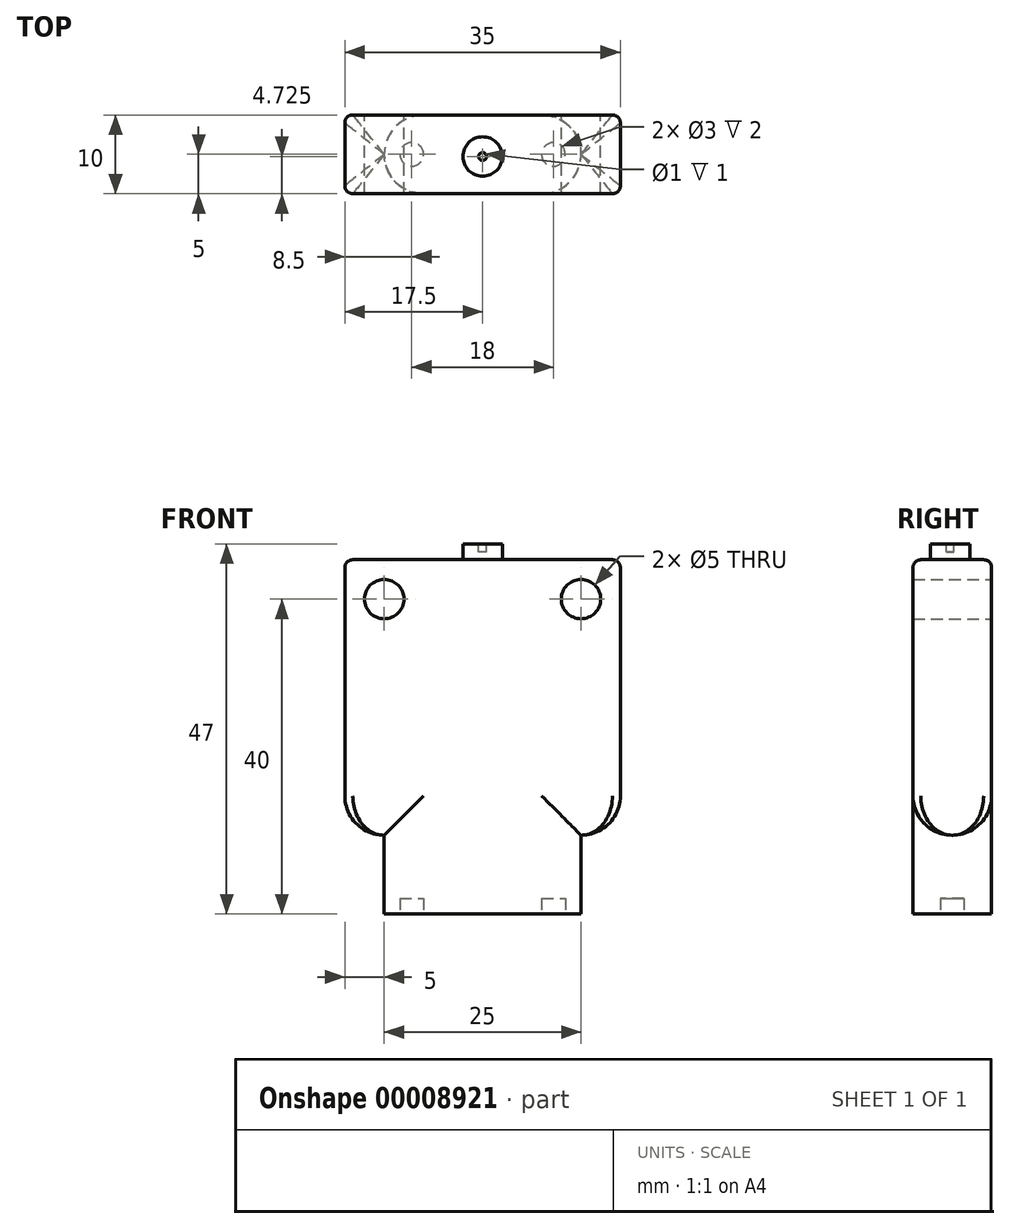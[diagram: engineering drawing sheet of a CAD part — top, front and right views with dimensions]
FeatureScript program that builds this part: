
annotation { "Feature Type Name" : "Feature", "Feature Type Description" : "" }
export const myFeature = defineFeature(function(context is Context, id is Id, definition is map)
    precondition{}
    {
        {
            var Q0;
            Q0=qCreatedBy(makeId("Top.planeOp"),FACE);
            var sketch = newSketch(context, id + "F0", { "sketchPlane" : qUnion([Q0])});
            skLineSegment(sketch, "E0.bottom", {"start": v(0, 0) * mm, "end": v(-25, 0) * mm});
            skLineSegment(sketch, "E0.top", {"start": v(0, 10) * mm, "end": v(-25, 10) * mm});
            skLineSegment(sketch, "E0.left", {"start": v(0, 0) * mm, "end": v(0, 10) * mm});
            skLineSegment(sketch, "E0.right", {"start": v(-25, 0) * mm, "end": v(-25, 10) * mm});
            skSolve(sketch);
        }
        {
            var Q0;
            Q0 = qSketchRegion(id + "F0", true);
            extrude(context, id + "F1", {"entities" : qUnion([Q0]), "depth" : 10 * mm});
        }
        {
            var Q0;
            Q0=makeQuery(id+"F1.opExtrude","CAP_FACE",FACE,{"disambiguationData":[OSD([sQuery(id+"F0.wireOp",EDGE,"E0.bottom"),sQuery(id+"F0.wireOp",EDGE,"E0.top"),sQuery(id+"F0.wireOp",EDGE,"E0.left"),sQuery(id+"F0.wireOp",EDGE,"E0.right")])],"isStart":true});
            var sketch = newSketch(context, id + "F2", { "sketchPlane" : qUnion([Q0])});
            skCircle(sketch, "E1", {"center": v(-21.5, -5) * mm, "radius": 1.5 * mm});
            skCircle(sketch, "E2", {"center": v(-3.5, -5) * mm, "radius": 1.5 * mm});
            skSolve(sketch);
        }
        {
            var Q0;
            Q0 = qSketchRegion(id + "F2", true);
            extrude(context, id + "F3", {"entities" : qUnion([Q0]), "operationType" : NewBodyOperationType.REMOVE, "oppositeDirection" : true, "depth" : 2 * mm});
        }
        {
            var Q0;
            Q0=makeQuery(id+"F1.opExtrude","SWEPT_EDGE",EDGE,{"disambiguationData":[OSD([sQuery(id+"F0.wireOp",EDGE,"E0.bottom"),sQuery(id+"F0.wireOp",EDGE,"E0.right")])]});
            var Q1;
            Q1=makeQuery(id+"F1.opExtrude","SWEPT_EDGE",EDGE,{"disambiguationData":[OSD([sQuery(id+"F0.wireOp",EDGE,"E0.top"),sQuery(id+"F0.wireOp",EDGE,"E0.right")])]});
            var Q2;
            Q2=makeQuery(id+"F1.opExtrude","SWEPT_EDGE",EDGE,{"disambiguationData":[OSD([sQuery(id+"F0.wireOp",EDGE,"E0.bottom"),sQuery(id+"F0.wireOp",EDGE,"E0.left")])]});
            var Q3;
            Q3=makeQuery(id+"F1.opExtrude","SWEPT_EDGE",EDGE,{"disambiguationData":[OSD([sQuery(id+"F0.wireOp",EDGE,"E0.top"),sQuery(id+"F0.wireOp",EDGE,"E0.left")])]});
            fillet(context, id + "F4", {"entities" : qUnion([Q0, Q1, Q2, Q3]), "radius" : 5 * mm, "tangentPropagation" : true, "allowEdgeOverflow" : false});
        }
        {
            var Q0;
            Q0=qCreatedBy(makeId("Front.planeOp"),FACE);
            var sketch = newSketch(context, id + "F5", { "sketchPlane" : qUnion([Q0])});
            skLineSegment(sketch, "E3.bottom", {"start": v(5, 10) * mm, "end": v(-30, 10) * mm});
            skLineSegment(sketch, "E3.top", {"start": v(5, 45) * mm, "end": v(-30, 45) * mm});
            skLineSegment(sketch, "E3.left", {"start": v(5, 10) * mm, "end": v(5, 45) * mm});
            skLineSegment(sketch, "E3.right", {"start": v(-30, 10) * mm, "end": v(-30, 45) * mm});
            skSolve(sketch);
        }
        {
            var Q0;
            Q0 = qSketchRegion(id + "F5", true);
            extrude(context, id + "F6", {"entities" : qUnion([Q0]), "operationType" : NewBodyOperationType.ADD, "oppositeDirection" : true, "depth" : 10 * mm});
        }
        {
            var Q0;
            {var subQ0=sQuery(id+"F5.wireOp",EDGE,"E3.bottom");var subQ1=sQuery(id+"F5.wireOp",EDGE,"E3.left");Q0=makeQuery(id+"F6.boolean.opBoolean","SPLIT",EDGE,{"disambiguationData":[TD([makeQuery(id+"F6.opExtrude","SWEPT_FACE",FACE,{"disambiguationData":[OSD([subQ1])]})])],"derivedFrom":makeQuery(id+"F6.opExtrude","CAP_EDGE",EDGE,{"disambiguationData":[OSD([subQ0])],"isStart":false})});}
            var Q1;
            {var subQ0=sQuery(id+"F5.wireOp",EDGE,"E3.bottom");var subQ1=sQuery(id+"F5.wireOp",EDGE,"E3.left");Q1=makeQuery(id+"F6.boolean.opBoolean","SPLIT",EDGE,{"disambiguationData":[TD([makeQuery(id+"F6.opExtrude","SWEPT_FACE",FACE,{"disambiguationData":[OSD([subQ1])]})])],"derivedFrom":makeQuery(id+"F6.opExtrude","CAP_EDGE",EDGE,{"disambiguationData":[OSD([subQ0])],"isStart":true})});}
            var Q2;
            {var subQ0=sQuery(id+"F5.wireOp",EDGE,"E3.bottom");var subQ1=sQuery(id+"F5.wireOp",EDGE,"E3.right");Q2=makeQuery(id+"F6.boolean.opBoolean","SPLIT",EDGE,{"disambiguationData":[TD([makeQuery(id+"F6.opExtrude","SWEPT_FACE",FACE,{"disambiguationData":[OSD([subQ1])]})])],"derivedFrom":makeQuery(id+"F6.opExtrude","CAP_EDGE",EDGE,{"disambiguationData":[OSD([subQ0])],"isStart":false})});}
            var Q3;
            {var subQ0=sQuery(id+"F5.wireOp",EDGE,"E3.bottom");var subQ1=sQuery(id+"F5.wireOp",EDGE,"E3.right");Q3=makeQuery(id+"F6.boolean.opBoolean","SPLIT",EDGE,{"disambiguationData":[TD([makeQuery(id+"F6.opExtrude","SWEPT_FACE",FACE,{"disambiguationData":[OSD([subQ1])]})])],"derivedFrom":makeQuery(id+"F6.opExtrude","CAP_EDGE",EDGE,{"disambiguationData":[OSD([subQ0])],"isStart":true})});}
            var Q4;
            Q4=makeQuery(id+"F6.opExtrude","SWEPT_EDGE",EDGE,{"disambiguationData":[OSD([sQuery(id+"F5.wireOp",EDGE,"E3.bottom"),sQuery(id+"F5.wireOp",EDGE,"E3.left")])]});
            var Q5;
            Q5=makeQuery(id+"F6.opExtrude","SWEPT_EDGE",EDGE,{"disambiguationData":[OSD([sQuery(id+"F5.wireOp",EDGE,"E3.bottom"),sQuery(id+"F5.wireOp",EDGE,"E3.right")])]});
            fillet(context, id + "F7", {"entities" : qUnion([Q0, Q1, Q2, Q3, Q4, Q5]), "radius" : 5 * mm, "tangentPropagation" : true, "allowEdgeOverflow" : false});
        }
        {
            var Q0;
            Q0=makeQuery(id+"F6.boolean.opBoolean","MERGE",FACE,{"derivedFrom":[makeQuery(id+"F1.opExtrude","SWEPT_FACE",FACE,{"disambiguationData":[OSD([sQuery(id+"F0.wireOp",EDGE,"E0.top")])]}),makeQuery(id+"F6.opExtrude","CAP_FACE",FACE,{"disambiguationData":[OSD([sQuery(id+"F5.wireOp",EDGE,"E3.bottom"),sQuery(id+"F5.wireOp",EDGE,"E3.top"),sQuery(id+"F5.wireOp",EDGE,"E3.left"),sQuery(id+"F5.wireOp",EDGE,"E3.right")])],"isStart":false})]});
            var sketch = newSketch(context, id + "F8", { "sketchPlane" : qUnion([Q0])});
            skCircle(sketch, "E4", {"center": v(0, 40) * mm, "radius": 2.5 * mm});
            skCircle(sketch, "E5", {"center": v(25, 40) * mm, "radius": 2.5 * mm});
            skSolve(sketch);
        }
        {
            var Q0;
            Q0 = qSketchRegion(id + "F8", true);
            extrude(context, id + "F9", {"entities" : qUnion([Q0]), "operationType" : NewBodyOperationType.REMOVE, "endBound" : BoundingType.THROUGH_ALL, "oppositeDirection" : true, "depth" : 25 * mm});
        }
        {
            var Q0;
            Q0=makeQuery(id+"F6.opExtrude","SWEPT_FACE",FACE,{"disambiguationData":[OSD([sQuery(id+"F5.wireOp",EDGE,"E3.top")])]});
            var sketch = newSketch(context, id + "F10", { "sketchPlane" : qUnion([Q0])});
            skCircle(sketch, "E6", {"center": v(-12.5, 4.73) * mm, "radius": 2.5 * mm});
            skSolve(sketch);
        }
        {
            var Q0;
            Q0 = qSketchRegion(id + "F10", true);
            extrude(context, id + "F11", {"entities" : qUnion([Q0]), "operationType" : NewBodyOperationType.ADD, "depth" : 2 * mm});
        }
        {
            var Q0;
            Q0=makeQuery(id+"F11.opExtrude","CAP_FACE",FACE,{"disambiguationData":[OSD([sQuery(id+"F10.wireOp",EDGE,"E6")])],"isStart":false});
            var sketch = newSketch(context, id + "F12", { "sketchPlane" : qUnion([Q0])});
            skCircle(sketch, "E7", {"center": v(-12.5, 4.73) * mm, "radius": 0.5 * mm});
            skSolve(sketch);
        }
        {
            var Q0;
            Q0 = qSketchRegion(id + "F12", true);
            extrude(context, id + "F13", {"entities" : qUnion([Q0]), "operationType" : NewBodyOperationType.REMOVE, "oppositeDirection" : true, "depth" : 1 * mm});
        }
        {
            var Q0;
            Q0=makeQuery(id+"F6.opExtrude","CAP_EDGE",EDGE,{"disambiguationData":[OSD([sQuery(id+"F5.wireOp",EDGE,"E3.top")])],"isStart":true});
            var Q1;
            Q1=makeQuery(id+"F6.opExtrude","CAP_EDGE",EDGE,{"disambiguationData":[OSD([sQuery(id+"F5.wireOp",EDGE,"E3.top")])],"isStart":false});
            var Q2;
            Q2=makeQuery(id+"F6.opExtrude","SWEPT_EDGE",EDGE,{"disambiguationData":[OSD([sQuery(id+"F5.wireOp",EDGE,"E3.top"),sQuery(id+"F5.wireOp",EDGE,"E3.left")])]});
            var Q3;
            Q3=makeQuery(id+"F6.opExtrude","SWEPT_EDGE",EDGE,{"disambiguationData":[OSD([sQuery(id+"F5.wireOp",EDGE,"E3.top"),sQuery(id+"F5.wireOp",EDGE,"E3.right")])]});
            var Q4;
            Q4=makeQuery(id+"F6.opExtrude","CAP_EDGE",EDGE,{"disambiguationData":[OSD([sQuery(id+"F5.wireOp",EDGE,"E3.left")])],"isStart":true});
            var Q5;
            Q5=makeQuery(id+"F6.opExtrude","CAP_EDGE",EDGE,{"disambiguationData":[OSD([sQuery(id+"F5.wireOp",EDGE,"E3.left")])],"isStart":false});
            var Q6;
            Q6=makeQuery(id+"F6.opExtrude","CAP_EDGE",EDGE,{"disambiguationData":[OSD([sQuery(id+"F5.wireOp",EDGE,"E3.right")])],"isStart":false});
            var Q7;
            Q7=makeQuery(id+"F6.opExtrude","CAP_EDGE",EDGE,{"disambiguationData":[OSD([sQuery(id+"F5.wireOp",EDGE,"E3.right")])],"isStart":true});
            fillet(context, id + "F14", {"entities" : qUnion([Q0, Q1, Q2, Q3, Q4, Q5, Q6, Q7]), "radius" : 1 * mm, "tangentPropagation" : true, "allowEdgeOverflow" : false});
        }
    });
